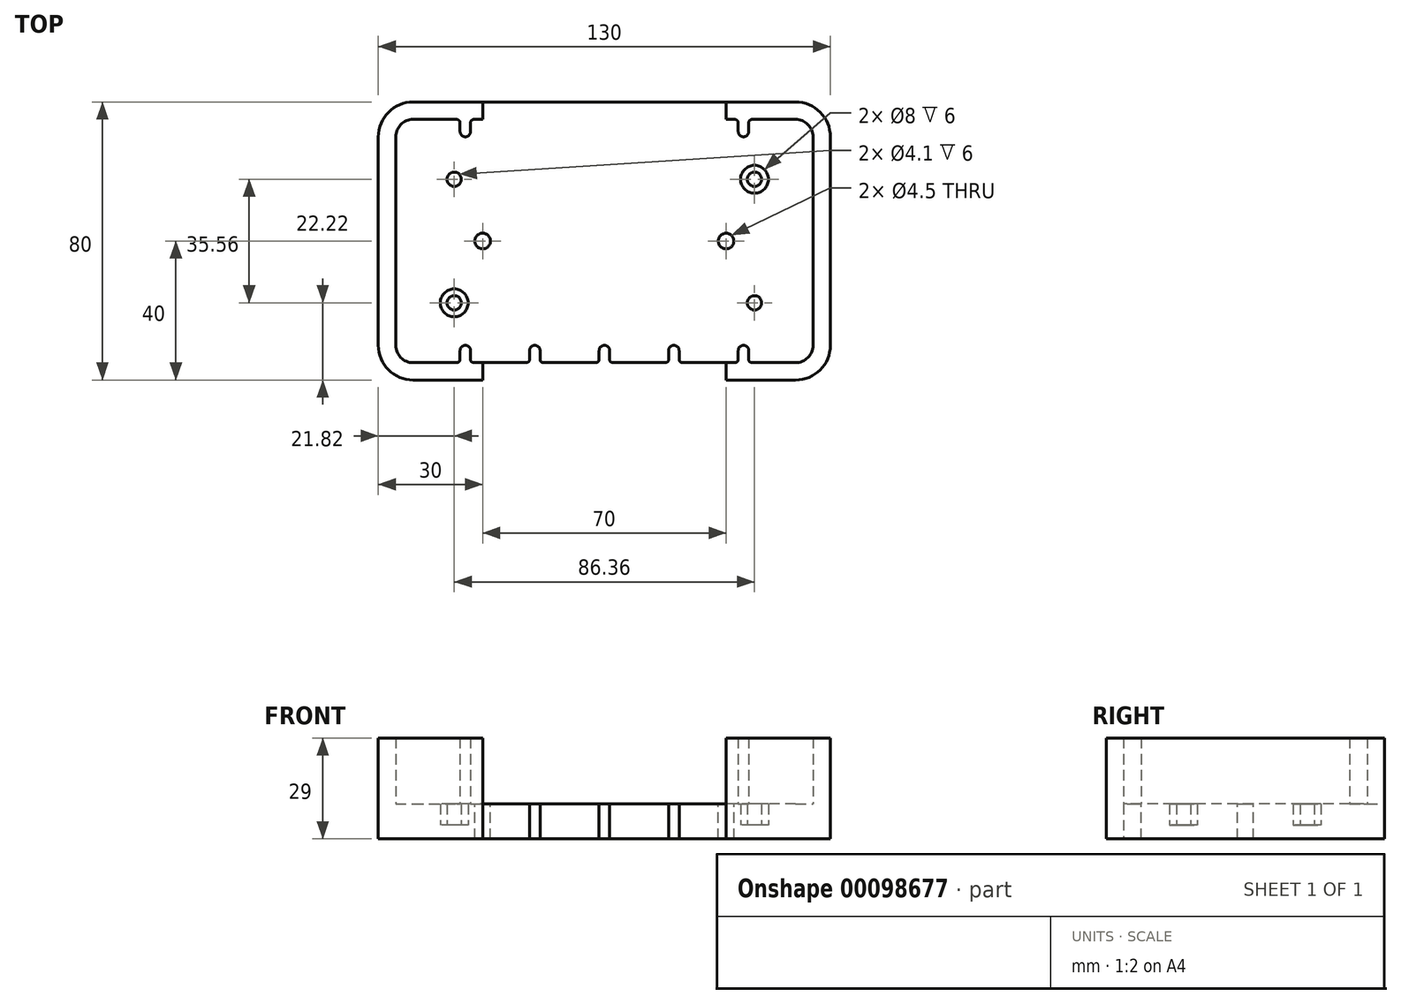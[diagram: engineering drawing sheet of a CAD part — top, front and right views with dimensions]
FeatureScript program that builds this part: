
annotation { "Feature Type Name" : "Feature", "Feature Type Description" : "" }
export const myFeature = defineFeature(function(context is Context, id is Id, definition is map)
    precondition{}
    {
        {
            var Q0;
            Q0=qCreatedBy(makeId("Top.planeOp"),FACE);
            var sketch = newSketch(context, id + "F0", { "sketchPlane" : qUnion([Q0])});
            skLineSegment(sketch, "E0.bottom", {"start": v(-50, 25) * mm, "end": v(50, 25) * mm, "construction": true});
            skLineSegment(sketch, "E0.top", {"start": v(-50, -25) * mm, "end": v(50, -25) * mm, "construction": true});
            skLineSegment(sketch, "E0.left", {"start": v(-50, 25) * mm, "end": v(-50, -25) * mm, "construction": true});
            skLineSegment(sketch, "E0.right", {"start": v(50, 25) * mm, "end": v(50, -25) * mm, "construction": true});
            skLineSegment(sketch, "E1.bottom", {"start": v(-37.5, 35) * mm, "end": v(-22.5, 35) * mm});
            skLineSegment(sketch, "E2", {"start": v(0, 25) * mm, "end": v(0, -25) * mm, "construction": true});
            skLineSegment(sketch, "E3", {"start": v(-50, 0) * mm, "end": v(50, 0) * mm, "construction": true});
            skPoint(sketch, "E4", {"position": v(-43.18, 17.78) * mm});
            skPoint(sketch, "E5.MirrorP", {"position": v(43.18, 17.78) * mm});
            skPoint(sketch, "E6.MirrorP", {"position": v(-43.18, -17.78) * mm});
            skPoint(sketch, "E7.MirrorP", {"position": v(43.18, -17.78) * mm});
            skLineSegment(sketch, "E8.MirrorCS", {"start": v(60, 35) * mm, "end": v(42.5, 35) * mm});
            skLineSegment(sketch, "E9.MirrorCS", {"start": v(-60, -35) * mm, "end": v(-42.5, -35) * mm});
            skLineSegment(sketch, "E10.MirrorCS", {"start": v(60, -35) * mm, "end": v(42.5, -35) * mm});
            skLineSegment(sketch, "E11", {"start": v(-60, 35) * mm, "end": v(-60, -35) * mm});
            skLineSegment(sketch, "E12", {"start": v(60, 35) * mm, "end": v(60, -35) * mm});
            skCircle(sketch, "E13", {"center": v(-43.18, 17.78) * mm, "radius": 2.05 * mm});
            skCircle(sketch, "E14.MirrorC", {"center": v(43.18, 17.78) * mm, "radius": 2.05 * mm});
            skCircle(sketch, "E15.MirrorC", {"center": v(-43.18, -17.78) * mm, "radius": 2.05 * mm});
            skCircle(sketch, "E16.MirrorC", {"center": v(43.18, -17.78) * mm, "radius": 2.05 * mm});
            skCircle(sketch, "E17", {"center": v(-43.18, 17.78) * mm, "radius": 4 * mm});
            skCircle(sketch, "E18.MirrorC", {"center": v(43.18, 17.78) * mm, "radius": 4 * mm});
            skCircle(sketch, "E19.MirrorC", {"center": v(-43.18, -17.78) * mm, "radius": 4 * mm});
            skCircle(sketch, "E20.MirrorC", {"center": v(43.18, -17.78) * mm, "radius": 4 * mm});
            skLineSegment(sketch, "E21.bottom", {"start": v(65, 40) * mm, "end": v(-65, 40) * mm});
            skLineSegment(sketch, "E21.top", {"start": v(65, -40) * mm, "end": v(-65, -40) * mm});
            skLineSegment(sketch, "E21.left", {"start": v(65, 40) * mm, "end": v(65, -40) * mm});
            skLineSegment(sketch, "E21.right", {"start": v(-65, 40) * mm, "end": v(-65, -40) * mm});
            skPoint(sketch, "E21.middle", {"position": v(0, 0) * mm});
            skLineSegment(sketch, "E22.left", {"start": v(-41.5, 34) * mm, "end": v(-41.5, 31.5) * mm});
            skLineSegment(sketch, "E22.right", {"start": v(-38.5, 34) * mm, "end": v(-38.5, 31.5) * mm});
            skArc(sketch, "E23", {"start": v(-41.5, 31.5) * mm, "mid": v(-40, 30) * mm, "end": v(-38.5, 31.5) * mm});
            skPoint(sketch, "E24.newPointB", {"position": v(-60, 35) * mm});
            skArc(sketch, "E24.filletArc", {"start": v(-37.5, 35) * mm, "mid": v(-38.2, 34.7) * mm, "end": v(-38.5, 34) * mm});
            skLineSegment(sketch, "E25", {"start": v(-60, 35) * mm, "end": v(-42.5, 35) * mm});
            skPoint(sketch, "E26.visualSharp", {"position": v(-41.5, 35) * mm});
            skArc(sketch, "E26.filletArc", {"start": v(-41.5, 34) * mm, "mid": v(-41.8, 34.7) * mm, "end": v(-42.5, 35) * mm});
            skLineSegment(sketch, "E27.left", {"start": v(-21.5, 34) * mm, "end": v(-21.5, 31.5) * mm});
            skLineSegment(sketch, "E27.right", {"start": v(-18.5, 34) * mm, "end": v(-18.5, 31.5) * mm});
            skArc(sketch, "E28", {"start": v(-21.5, 31.5) * mm, "mid": v(-20, 30) * mm, "end": v(-18.5, 31.5) * mm});
            skArc(sketch, "E29.filletArc", {"start": v(-17.5, 35) * mm, "mid": v(-18.2, 34.7) * mm, "end": v(-18.5, 34) * mm});
            skPoint(sketch, "E30.visualSharp", {"position": v(-21.5, 51.22) * mm});
            skArc(sketch, "E30.filletArc", {"start": v(-21.5, 34) * mm, "mid": v(-21.8, 34.7) * mm, "end": v(-22.5, 35) * mm});
            skLineSegment(sketch, "E31", {"start": v(-40, 31.5) * mm, "end": v(-60, 31.5) * mm, "construction": true});
            skLineSegment(sketch, "E32", {"start": v(-40, 31.5) * mm, "end": v(-20, 31.5) * mm, "construction": true});
            skLineSegment(sketch, "E33", {"start": v(0, 25) * mm, "end": v(0, 35) * mm, "construction": true});
            skLineSegment(sketch, "E34", {"start": v(-20, 31.5) * mm, "end": v(0, 31.5) * mm, "construction": true});
            skArc(sketch, "E35.MirrorCS", {"start": v(21.5, 31.5) * mm, "mid": v(20, 30) * mm, "end": v(18.5, 31.5) * mm});
            skArc(sketch, "E36.MirrorCS", {"start": v(41.5, 31.5) * mm, "mid": v(40, 30) * mm, "end": v(38.5, 31.5) * mm});
            skLineSegment(sketch, "E37.MirrorCS", {"start": v(18.5, 34) * mm, "end": v(18.5, 31.5) * mm});
            skLineSegment(sketch, "E38.MirrorCS", {"start": v(21.5, 34) * mm, "end": v(21.5, 31.5) * mm});
            skArc(sketch, "E39.MirrorCS", {"start": v(21.5, 34) * mm, "mid": v(21.8, 34.7) * mm, "end": v(22.5, 35) * mm});
            skArc(sketch, "E40.MirrorCS", {"start": v(17.5, 35) * mm, "mid": v(18.2, 34.7) * mm, "end": v(18.5, 34) * mm});
            skLineSegment(sketch, "E41.MirrorCS", {"start": v(38.5, 34) * mm, "end": v(38.5, 31.5) * mm});
            skLineSegment(sketch, "E42.MirrorCS", {"start": v(41.5, 34) * mm, "end": v(41.5, 31.5) * mm});
            skArc(sketch, "E43.MirrorCS", {"start": v(37.5, 35) * mm, "mid": v(38.2, 34.7) * mm, "end": v(38.5, 34) * mm});
            skArc(sketch, "E44.MirrorCS", {"start": v(41.5, 34) * mm, "mid": v(41.8, 34.7) * mm, "end": v(42.5, 35) * mm});
            skLineSegment(sketch, "E45.trimOffspring", {"start": v(-17.5, 35) * mm, "end": v(-2.5, 35) * mm});
            skLineSegment(sketch, "E46.trimOffspring", {"start": v(17.5, 35) * mm, "end": v(2.5, 35) * mm});
            skLineSegment(sketch, "E47.trimOffspring", {"start": v(37.5, 35) * mm, "end": v(22.5, 35) * mm});
            skLineSegment(sketch, "E48.left", {"start": v(-1.5, 34) * mm, "end": v(-1.5, 31.5) * mm});
            skLineSegment(sketch, "E48.right", {"start": v(1.5, 34) * mm, "end": v(1.5, 31.5) * mm});
            skArc(sketch, "E49", {"start": v(-1.5, 31.5) * mm, "mid": v(0, 30) * mm, "end": v(1.5, 31.5) * mm});
            skPoint(sketch, "E50.newPointB", {"position": v(0, 35) * mm});
            skArc(sketch, "E50.filletArc", {"start": v(2.5, 35) * mm, "mid": v(1.8, 34.7) * mm, "end": v(1.5, 34) * mm});
            skArc(sketch, "E51.filletArc", {"start": v(-1.5, 34) * mm, "mid": v(-1.8, 34.7) * mm, "end": v(-2.5, 35) * mm});
            skLineSegment(sketch, "E52", {"start": v(-41.5, 31.5) * mm, "end": v(-38.5, 31.5) * mm, "construction": true});
            skLineSegment(sketch, "E53", {"start": v(-21.5, 31.5) * mm, "end": v(-18.5, 31.5) * mm, "construction": true});
            skLineSegment(sketch, "E54", {"start": v(-1.5, 31.5) * mm, "end": v(1.5, 31.5) * mm, "construction": true});
            skArc(sketch, "E55.MirrorCS", {"start": v(-41.5, -34) * mm, "mid": v(-41.8, -34.7) * mm, "end": v(-42.5, -35) * mm});
            skLineSegment(sketch, "E56.MirrorCS", {"start": v(-41.5, -34) * mm, "end": v(-41.5, -31.5) * mm});
            skArc(sketch, "E57.MirrorCS", {"start": v(-41.5, -31.5) * mm, "mid": v(-40, -30) * mm, "end": v(-38.5, -31.5) * mm});
            skLineSegment(sketch, "E58.MirrorCS", {"start": v(-38.5, -34) * mm, "end": v(-38.5, -31.5) * mm});
            skArc(sketch, "E59.MirrorCS", {"start": v(-37.5, -35) * mm, "mid": v(-38.2, -34.7) * mm, "end": v(-38.5, -34) * mm});
            skArc(sketch, "E60.MirrorCS", {"start": v(-21.5, -34) * mm, "mid": v(-21.8, -34.7) * mm, "end": v(-22.5, -35) * mm});
            skLineSegment(sketch, "E61.MirrorCS", {"start": v(-21.5, -34) * mm, "end": v(-21.5, -31.5) * mm});
            skArc(sketch, "E62.MirrorCS", {"start": v(-21.5, -31.5) * mm, "mid": v(-20, -30) * mm, "end": v(-18.5, -31.5) * mm});
            skLineSegment(sketch, "E63.MirrorCS", {"start": v(-18.5, -34) * mm, "end": v(-18.5, -31.5) * mm});
            skArc(sketch, "E64.MirrorCS", {"start": v(-17.5, -35) * mm, "mid": v(-18.2, -34.7) * mm, "end": v(-18.5, -34) * mm});
            skArc(sketch, "E65.MirrorCS", {"start": v(-1.5, -34) * mm, "mid": v(-1.8, -34.7) * mm, "end": v(-2.5, -35) * mm});
            skLineSegment(sketch, "E66.MirrorCS", {"start": v(-1.5, -34) * mm, "end": v(-1.5, -31.5) * mm});
            skArc(sketch, "E67.MirrorCS", {"start": v(-1.5, -31.5) * mm, "mid": v(0, -30) * mm, "end": v(1.5, -31.5) * mm});
            skLineSegment(sketch, "E68.MirrorCS", {"start": v(1.5, -34) * mm, "end": v(1.5, -31.5) * mm});
            skArc(sketch, "E69.MirrorCS", {"start": v(2.5, -35) * mm, "mid": v(1.8, -34.7) * mm, "end": v(1.5, -34) * mm});
            skArc(sketch, "E70.MirrorCS", {"start": v(17.5, -35) * mm, "mid": v(18.2, -34.7) * mm, "end": v(18.5, -34) * mm});
            skLineSegment(sketch, "E71.MirrorCS", {"start": v(18.5, -34) * mm, "end": v(18.5, -31.5) * mm});
            skArc(sketch, "E72.MirrorCS", {"start": v(21.5, -31.5) * mm, "mid": v(20, -30) * mm, "end": v(18.5, -31.5) * mm});
            skLineSegment(sketch, "E73.MirrorCS", {"start": v(21.5, -34) * mm, "end": v(21.5, -31.5) * mm});
            skArc(sketch, "E74.MirrorCS", {"start": v(21.5, -34) * mm, "mid": v(21.8, -34.7) * mm, "end": v(22.5, -35) * mm});
            skArc(sketch, "E75.MirrorCS", {"start": v(37.5, -35) * mm, "mid": v(38.2, -34.7) * mm, "end": v(38.5, -34) * mm});
            skLineSegment(sketch, "E76.MirrorCS", {"start": v(38.5, -34) * mm, "end": v(38.5, -31.5) * mm});
            skArc(sketch, "E77.MirrorCS", {"start": v(41.5, -31.5) * mm, "mid": v(40, -30) * mm, "end": v(38.5, -31.5) * mm});
            skLineSegment(sketch, "E78.MirrorCS", {"start": v(41.5, -34) * mm, "end": v(41.5, -31.5) * mm});
            skArc(sketch, "E79.MirrorCS", {"start": v(41.5, -34) * mm, "mid": v(41.8, -34.7) * mm, "end": v(42.5, -35) * mm});
            skLineSegment(sketch, "E80.trimOffspring", {"start": v(-37.5, -35) * mm, "end": v(-22.5, -35) * mm});
            skLineSegment(sketch, "E81.trimOffspring", {"start": v(-17.5, -35) * mm, "end": v(-2.5, -35) * mm});
            skLineSegment(sketch, "E82.trimOffspring", {"start": v(17.5, -35) * mm, "end": v(2.5, -35) * mm});
            skLineSegment(sketch, "E83.trimOffspring", {"start": v(37.5, -35) * mm, "end": v(22.5, -35) * mm});
            skPoint(sketch, "E84.orphan", {"position": v(0, -35) * mm});
            skCircle(sketch, "E85", {"center": v(-35, 0) * mm, "radius": 2.25 * mm});
            skCircle(sketch, "E86.MirrorC", {"center": v(35, 0) * mm, "radius": 2.25 * mm});
            skLineSegment(sketch, "E87.left", {"start": v(-35, -35) * mm, "end": v(-35, -40) * mm});
            skLineSegment(sketch, "E87.right", {"start": v(35, -35) * mm, "end": v(35, -40) * mm});
            skLineSegment(sketch, "E88.MirrorCS", {"start": v(-35, 35) * mm, "end": v(-35, 40) * mm});
            skLineSegment(sketch, "E89.MirrorCS", {"start": v(35, 35) * mm, "end": v(35, 40) * mm});
            skSolve(sketch);
        }
        {
            var Q0;
            Q0=makeQuery(id+"F0.imprint","IMPRINT",FACE,{"disambiguationData":[TD([[makeQuery(id+"F0.imprint","IMPRINT",EDGE,{"derivedFrom":sQuery(id+"F0.wireOp",EDGE,"E1.bottom")}),1.0]])]});
            var Q1;
            Q1=makeQuery(id+"F0.imprint","IMPRINT",FACE,{"disambiguationData":[TD([[makeQuery(id+"F0.imprint","IMPRINT",EDGE,{"derivedFrom":sQuery(id+"F0.wireOp",EDGE,"E8.MirrorCS")}),-1.0]])]});
            extrude(context, id + "F1", {"entities" : qUnion([Q0, Q1]), "depth" : 25 * mm});
        }
        {
            var Q0;
            Q0=makeQuery(id+"F0.imprint","IMPRINT",FACE,{"disambiguationData":[TD([[makeQuery(id+"F0.imprint","IMPRINT",EDGE,{"derivedFrom":sQuery(id+"F0.wireOp",EDGE,"E14.MirrorC")}),1.0]])]});
            var Q1;
            Q1=makeQuery(id+"F0.imprint","IMPRINT",FACE,{"disambiguationData":[TD([[makeQuery(id+"F0.imprint","IMPRINT",EDGE,{"derivedFrom":sQuery(id+"F0.wireOp",EDGE,"E15.MirrorC")}),1.0]])]});
            var Q2;
            Q2=makeQuery(id+"F0.imprint","IMPRINT",FACE,{"disambiguationData":[TD([[makeQuery(id+"F0.imprint","IMPRINT",EDGE,{"derivedFrom":sQuery(id+"F0.wireOp",EDGE,"E16.MirrorC")}),-1.0]])]});
            var Q3;
            Q3=makeQuery(id+"F0.imprint","IMPRINT",FACE,{"disambiguationData":[TD([[makeQuery(id+"F0.imprint","IMPRINT",EDGE,{"derivedFrom":sQuery(id+"F0.wireOp",EDGE,"E1.bottom")}),-1.0]])]});
            var Q4;
            Q4=makeQuery(id+"F0.imprint","IMPRINT",FACE,{"disambiguationData":[TD([[makeQuery(id+"F0.imprint","IMPRINT",EDGE,{"derivedFrom":sQuery(id+"F0.wireOp",EDGE,"E1.bottom")}),1.0]])]});
            var Q5;
            Q5=makeQuery(id+"F0.imprint","IMPRINT",FACE,{"disambiguationData":[TD([[makeQuery(id+"F0.imprint","IMPRINT",EDGE,{"derivedFrom":sQuery(id+"F0.wireOp",EDGE,"E15.MirrorC")}),-1.0]])]});
            var Q6;
            Q6=makeQuery(id+"F0.imprint","IMPRINT",FACE,{"disambiguationData":[TD([[makeQuery(id+"F0.imprint","IMPRINT",EDGE,{"derivedFrom":sQuery(id+"F0.wireOp",EDGE,"E16.MirrorC")}),1.0]])]});
            var Q7;
            Q7=makeQuery(id+"F0.imprint","IMPRINT",FACE,{"disambiguationData":[TD([[makeQuery(id+"F0.imprint","IMPRINT",EDGE,{"derivedFrom":sQuery(id+"F0.wireOp",EDGE,"E14.MirrorC")}),-1.0]])]});
            var Q8;
            Q8=makeQuery(id+"F0.imprint","IMPRINT",FACE,{"disambiguationData":[TD([[makeQuery(id+"F0.imprint","IMPRINT",EDGE,{"derivedFrom":sQuery(id+"F0.wireOp",EDGE,"E13")}),-1.0]])]});
            var Q9;
            Q9=makeQuery(id+"F0.imprint","IMPRINT",FACE,{"disambiguationData":[TD([[makeQuery(id+"F0.imprint","IMPRINT",EDGE,{"derivedFrom":sQuery(id+"F0.wireOp",EDGE,"E13")}),1.0]])]});
            extrude(context, id + "F2", {"entities" : qUnion([Q0, Q1, Q2, Q3, Q4, Q5, Q6, Q7, Q8, Q9]), "operationType" : NewBodyOperationType.ADD, "oppositeDirection" : true, "depth" : 4 * mm});
        }
        {
            var Q0;
            Q0=makeQuery(id+"F0.imprint","IMPRINT",FACE,{"disambiguationData":[TD([[makeQuery(id+"F0.imprint","IMPRINT",EDGE,{"derivedFrom":sQuery(id+"F0.wireOp",EDGE,"E13")}),-1.0]])]});
            var Q1;
            Q1=makeQuery(id+"F0.imprint","IMPRINT",FACE,{"disambiguationData":[TD([[makeQuery(id+"F0.imprint","IMPRINT",EDGE,{"derivedFrom":sQuery(id+"F0.wireOp",EDGE,"E14.MirrorC")}),1.0]])]});
            var Q2;
            Q2=makeQuery(id+"F0.imprint","IMPRINT",FACE,{"disambiguationData":[TD([[makeQuery(id+"F0.imprint","IMPRINT",EDGE,{"derivedFrom":sQuery(id+"F0.wireOp",EDGE,"E15.MirrorC")}),1.0]])]});
            var Q3;
            Q3=makeQuery(id+"F0.imprint","IMPRINT",FACE,{"disambiguationData":[TD([[makeQuery(id+"F0.imprint","IMPRINT",EDGE,{"derivedFrom":sQuery(id+"F0.wireOp",EDGE,"E16.MirrorC")}),-1.0]])]});
            extrude(context, id + "F3", {"entities" : qUnion([Q0, Q1, Q2, Q3]), "operationType" : NewBodyOperationType.ADD, "depth" : 6 * mm});
        }
        {
            var Q0;
            {var subQ0=sQuery(id+"F0.wireOp",EDGE,"E60.MirrorCS");Q0=makeQuery(id+"F0.imprint","IMPRINT",FACE,{"disambiguationData":[TD([[makeQuery(id+"F0.imprint","IMPRINT",EDGE,{"derivedFrom":subQ0}),1.0]])]});}
            var Q1;
            Q1=makeQuery(id+"F0.imprint","IMPRINT",FACE,{"disambiguationData":[TD([[makeQuery(id+"F0.imprint","IMPRINT",EDGE,{"derivedFrom":sQuery(id+"F0.wireOp",EDGE,"E8.MirrorCS")}),-1.0]])]});
            var Q2;
            Q2=makeQuery(id+"F0.imprint","IMPRINT",FACE,{"disambiguationData":[TD([[makeQuery(id+"F0.imprint","IMPRINT",EDGE,{"derivedFrom":sQuery(id+"F0.wireOp",EDGE,"E27.left")}),1.0]])]});
            var Q3;
            Q3=makeQuery(id+"F3.opExtrude","CAP_FACE",FACE,{"disambiguationData":[OSD([sQuery(id+"F0.wireOp",EDGE,"E13"),sQuery(id+"F0.wireOp",EDGE,"E17")])],"isStart":false});
            var Q4;
            Q4=makeQuery(id+"F2.opExtrude","CAP_FACE",FACE,{"disambiguationData":[OSD([sQuery(id+"F0.wireOp",EDGE,"E21.bottom"),sQuery(id+"F0.wireOp",EDGE,"E21.top"),sQuery(id+"F0.wireOp",EDGE,"E21.left"),sQuery(id+"F0.wireOp",EDGE,"E21.right"),sQuery(id+"F0.wireOp",EDGE,"E60.MirrorCS"),sQuery(id+"F0.wireOp",EDGE,"E61.MirrorCS"),sQuery(id+"F0.wireOp",EDGE,"E62.MirrorCS"),sQuery(id+"F0.wireOp",EDGE,"E63.MirrorCS"),sQuery(id+"F0.wireOp",EDGE,"E64.MirrorCS"),sQuery(id+"F0.wireOp",EDGE,"E65.MirrorCS"),sQuery(id+"F0.wireOp",EDGE,"E66.MirrorCS"),sQuery(id+"F0.wireOp",EDGE,"E67.MirrorCS"),sQuery(id+"F0.wireOp",EDGE,"E68.MirrorCS"),sQuery(id+"F0.wireOp",EDGE,"E69.MirrorCS"),sQuery(id+"F0.wireOp",EDGE,"E70.MirrorCS"),sQuery(id+"F0.wireOp",EDGE,"E71.MirrorCS"),sQuery(id+"F0.wireOp",EDGE,"E72.MirrorCS"),sQuery(id+"F0.wireOp",EDGE,"E73.MirrorCS"),sQuery(id+"F0.wireOp",EDGE,"E74.MirrorCS"),sQuery(id+"F0.wireOp",EDGE,"E80.trimOffspring"),sQuery(id+"F0.wireOp",EDGE,"E81.trimOffspring"),sQuery(id+"F0.wireOp",EDGE,"E82.trimOffspring"),sQuery(id+"F0.wireOp",EDGE,"E83.trimOffspring"),sQuery(id+"F0.wireOp",EDGE,"E85"),sQuery(id+"F0.wireOp",EDGE,"E86.MirrorC"),sQuery(id+"F0.wireOp",EDGE,"E87.left"),sQuery(id+"F0.wireOp",EDGE,"E87.right")])],"isStart":false});
            extrude(context, id + "F4", {"entities" : qUnion([Q0, Q1, Q2]), "operationType" : NewBodyOperationType.ADD, "endBound" : BoundingType.UP_TO_SURFACE, "endBoundEntityFace" : qUnion([Q3]), "depth" : 6 * mm, "hasSecondDirection" : true, "secondDirectionBound" : SecondDirectionBoundingType.UP_TO_SURFACE, "secondDirectionOppositeDirection" : true, "secondDirectionBoundEntityFace" : qUnion([Q4]), "secondDirectionDepth" : 25 * mm});
        }
        {
            var Q0;
            {var subQ0=sQuery(id+"F0.wireOp",EDGE,"E21.right");var subQ1=sQuery(id+"F0.wireOp",EDGE,"E21.top");Q0=makeQuery(id+"F2.boolean.opBoolean","MERGE",EDGE,{"derivedFrom":[makeQuery(id+"F1.opExtrude","SWEPT_EDGE",EDGE,{"disambiguationData":[OSD([subQ1,subQ0])]}),makeQuery(id+"F2.opExtrude","SWEPT_EDGE",EDGE,{"disambiguationData":[OSD([subQ1,subQ0])]})]});}
            var Q1;
            {var subQ0=sQuery(id+"F0.wireOp",EDGE,"E21.right");var subQ1=sQuery(id+"F0.wireOp",EDGE,"E21.bottom");Q1=makeQuery(id+"F2.boolean.opBoolean","MERGE",EDGE,{"derivedFrom":[makeQuery(id+"F1.opExtrude","SWEPT_EDGE",EDGE,{"disambiguationData":[OSD([subQ1,subQ0])]}),makeQuery(id+"F2.opExtrude","SWEPT_EDGE",EDGE,{"disambiguationData":[OSD([subQ1,subQ0])]})]});}
            var Q2;
            {var subQ0=sQuery(id+"F0.wireOp",EDGE,"E21.right");var subQ1=sQuery(id+"F0.wireOp",EDGE,"E21.bottom");Q2=makeQuery(id+"F2.boolean.opBoolean","MERGE",EDGE,{"derivedFrom":[makeQuery(id+"F1.opExtrude","SWEPT_EDGE",EDGE,{"disambiguationData":[OSD([subQ1,subQ0])]}),makeQuery(id+"F2.opExtrude","SWEPT_EDGE",EDGE,{"disambiguationData":[OSD([subQ1,subQ0])]})]});}
            var Q3;
            {var subQ0=sQuery(id+"F0.wireOp",EDGE,"E21.right");var subQ1=sQuery(id+"F0.wireOp",EDGE,"E21.top");Q3=makeQuery(id+"F2.boolean.opBoolean","MERGE",EDGE,{"derivedFrom":[makeQuery(id+"F1.opExtrude","SWEPT_EDGE",EDGE,{"disambiguationData":[OSD([subQ1,subQ0])]}),makeQuery(id+"F2.opExtrude","SWEPT_EDGE",EDGE,{"disambiguationData":[OSD([subQ1,subQ0])]})]});}
            var Q4;
            {var subQ0=sQuery(id+"F0.wireOp",EDGE,"E21.left");var subQ1=sQuery(id+"F0.wireOp",EDGE,"E21.top");Q4=makeQuery(id+"F4.boolean.opBoolean","MERGE",EDGE,{"derivedFrom":[makeQuery(id+"F1.opExtrude","SWEPT_EDGE",EDGE,{"disambiguationData":[OSD([subQ1,subQ0])]}),makeQuery(id+"F4.opExtrude","TWEAK_EDGE",EDGE,{"derivedFrom":[makeQuery(id+"F0.imprint","IMPRINT",EDGE,{"disambiguationData":[TD([[makeQuery(id+"F0.imprint","INTERSECT",VERTEX,{"derivedFrom":[subQ1,subQ0]}),-1.0]])],"derivedFrom":subQ1}),makeQuery(id+"F0.imprint","IMPRINT",EDGE,{"disambiguationData":[TD([[makeQuery(id+"F0.imprint","INTERSECT",VERTEX,{"derivedFrom":[subQ1,sQuery(id+"F0.wireOp",EDGE,"E87.left")]}),1.0]])],"derivedFrom":subQ1}),makeQuery(id+"F0.imprint","IMPRINT",EDGE,{"derivedFrom":subQ0})]})]});}
            var Q5;
            {var subQ0=sQuery(id+"F0.wireOp",EDGE,"E21.left");var subQ1=sQuery(id+"F0.wireOp",EDGE,"E21.bottom");Q5=makeQuery(id+"F4.boolean.opBoolean","MERGE",EDGE,{"derivedFrom":[makeQuery(id+"F1.opExtrude","SWEPT_EDGE",EDGE,{"disambiguationData":[OSD([subQ1,subQ0])]}),makeQuery(id+"F4.opExtrude","TWEAK_EDGE",EDGE,{"derivedFrom":[makeQuery(id+"F0.imprint","IMPRINT",EDGE,{"disambiguationData":[TD([[makeQuery(id+"F0.imprint","INTERSECT",VERTEX,{"derivedFrom":[subQ1,subQ0]}),-1.0]])],"derivedFrom":subQ1}),makeQuery(id+"F0.imprint","IMPRINT",EDGE,{"disambiguationData":[TD([[makeQuery(id+"F0.imprint","INTERSECT",VERTEX,{"derivedFrom":[subQ1,sQuery(id+"F0.wireOp",EDGE,"E88.MirrorCS")]}),1.0]])],"derivedFrom":subQ1}),makeQuery(id+"F0.imprint","IMPRINT",EDGE,{"derivedFrom":subQ0})]})]});}
            fillet(context, id + "F5", {"entities" : qUnion([Q0, Q1, Q2, Q3, Q4, Q5]), "radius" : 10 * mm, "tangentPropagation" : true, "allowEdgeOverflow" : false});
        }
        {
            var Q0;
            Q0=makeQuery(id+"F1.opExtrude","SWEPT_EDGE",EDGE,{"disambiguationData":[OSD([sQuery(id+"F0.wireOp",EDGE,"E11"),sQuery(id+"F0.wireOp",EDGE,"E25")])]});
            var Q1;
            Q1=makeQuery(id+"F1.opExtrude","SWEPT_EDGE",EDGE,{"disambiguationData":[OSD([sQuery(id+"F0.wireOp",EDGE,"E8.MirrorCS"),sQuery(id+"F0.wireOp",EDGE,"E12")])]});
            var Q2;
            Q2=makeQuery(id+"F1.opExtrude","SWEPT_EDGE",EDGE,{"disambiguationData":[OSD([sQuery(id+"F0.wireOp",EDGE,"E10.MirrorCS"),sQuery(id+"F0.wireOp",EDGE,"E12")])]});
            var Q3;
            Q3=makeQuery(id+"F1.opExtrude","SWEPT_EDGE",EDGE,{"disambiguationData":[OSD([sQuery(id+"F0.wireOp",EDGE,"E9.MirrorCS"),sQuery(id+"F0.wireOp",EDGE,"E11")])]});
            fillet(context, id + "F6", {"entities" : qUnion([Q0, Q1, Q2, Q3]), "radius" : 5 * mm, "tangentPropagation" : true, "allowEdgeOverflow" : false});
        }
    });
